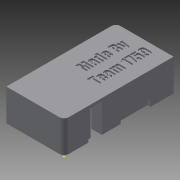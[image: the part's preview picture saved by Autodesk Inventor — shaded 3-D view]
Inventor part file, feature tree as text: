
AUTODESK INVENTOR PART (.ipt)
format: ipt  version: 2015 (Build 190159000, 159)  size: 555,008 bytes
history: native  units: in
note: dims shown in document units (in); Inventor stores cm internally (conversion verified against a paired STEP export)
features: extrude x10, sketch x9, projected_geometry x3, fillet x2
ambient origin geometry x8: Origin, YZ Plane, XZ Plane, XY Plane, X Axis, Y Axis, Z Axis, Center Point
bodies: Solid1 (feature_tree)
feature tree (24):
  extrude  "Extrusion1"  Depth=0.966in
  sketch  "Sketch2"  dims[d5=0.075in d6=0.1in d7=0.1in]
  fillet  "Fillet1"  Radius=0.533in
  fillet  "Fillet2"  Radius=0.075in
  extrude  "Extrusion2"  Depth=0.1in
  extrude  "Extrusion3"  Depth=0.125in
  extrude  "Extrusion4"  Depth=0.1in
  sketch  "Sketch6"  dims[d15=0.1in d16=0.1in]
  extrude  "Extrusion5"  Depth=0.1in
  sketch  "Sketch7"  dims[d17=0.1in d18=0.483in]
  extrude  "Extrusion7"  Depth=0.483in
  extrude  "Extrusion8"  Depth=0.1in
  extrude  "Extrusion9"  Depth=0.1in
  extrude  "Extrusion10"  Depth=0.5in
  extrude  "Extrusion11"  Depth=0.45in
  sketch  "Sketch1"  dims[d0=1.833in d1=0.966in d2=0.533in d3=0.0in d4=0.075in]
  sketch  "Sketch4"  dims[d8=0.1in d9=0.1in d11=0.125in]
  sketch  "Sketch5"  dims[d13=0.175in d14=0.1in]
  sketch  "Sketch8"  dims[d19=0.0in d20=0.1in]
  projected_geometry  "Projected Loop1"
  sketch  "Sketch9"  dims[d21=0.24in d22=0.1in]
  projected_geometry  "Projected Loop2"
  sketch  "Sketch10"  dims[d23=0.535in d24=0.5in d25=0.45in d26=0.9in d27=0.533in d28=0.0in d29=0.279in d30=0.185in d32=0.3in d33=0.1in d34=0.533in d35=0.0in d36=0.1718in d37=1.2625in d38=0.025in d39=0.0in d40=0.05in d41=0.1in d42=0.025in d43=0.025in d46=0.05in d47=0.025in d48=0.0in d49=0.025in d50=0.0in d51=0.1in d52=0.5in d53=0.05in d54=0.0in d55=0.1in d56=0.0in d57=1.0in d58=0.5in d59=0.025in d60=0.0in d61=0.375in]
  projected_geometry  "Projected Loop3"
